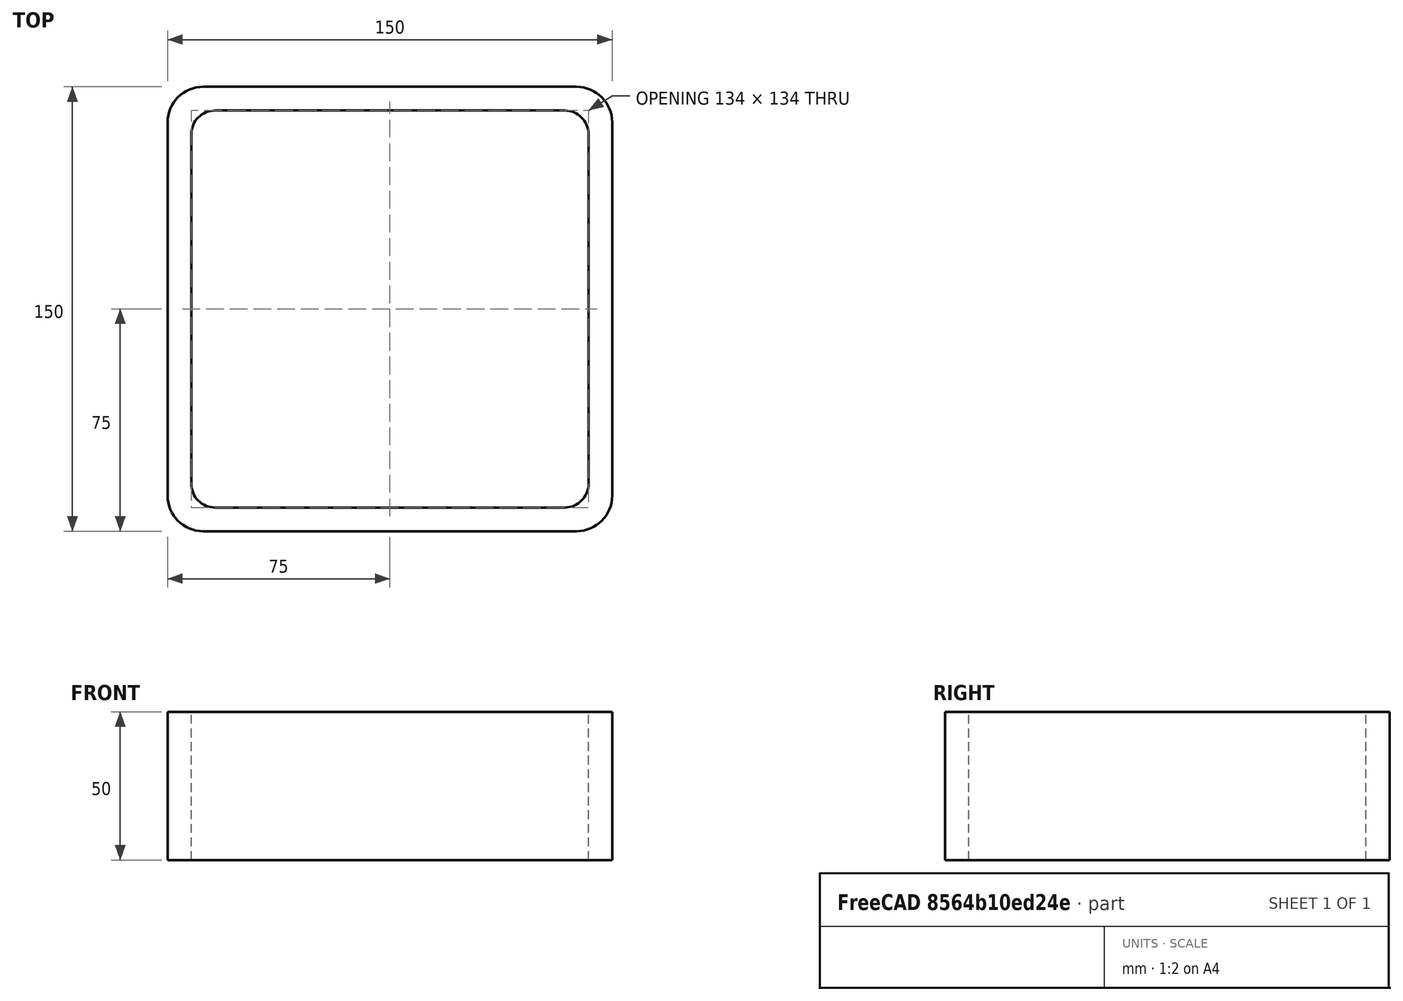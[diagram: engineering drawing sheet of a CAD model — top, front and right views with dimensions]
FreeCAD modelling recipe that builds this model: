
FCSTD DOCUMENT  (FreeCAD 0.15R4671 (Git))
Label: Square hollow section 150x150x8 EN10219 S235JRH
License: All rights reserved
LicenseURL: http://en.wikipedia.org/wiki/All_rights_reserved
objects: Sketcher::SketchObject×1, Part::Extrusion×1
note: 2 computed .brp shape members not serialized (recipe doc carries the construction recipe); baked Part::Feature solids carry a one-line shape summary decoded from their .brp

FEATURE [Sketcher::SketchObject] Sketch
  sketch-geometry (16):
    g0: LineSegment StartX=-59 StartY=67 StartZ=0 EndX=59 EndY=67 EndZ=0
    g1: LineSegment StartX=67 StartY=59 StartZ=0 EndX=67 EndY=-59 EndZ=0
    g2: LineSegment StartX=59 StartY=-67 StartZ=0 EndX=-59 EndY=-67 EndZ=0
    g3: LineSegment StartX=-67 StartY=-59 StartZ=0 EndX=-67 EndY=59 EndZ=0
    g4: LineSegment StartX=-63 StartY=75 StartZ=0 EndX=63 EndY=75 EndZ=0
    g5: LineSegment StartX=75 StartY=63 StartZ=0 EndX=75 EndY=-63 EndZ=0
    g6: LineSegment StartX=63 StartY=-75 StartZ=0 EndX=-63 EndY=-75 EndZ=0
    g7: LineSegment StartX=-75 StartY=-63 StartZ=0 EndX=-75 EndY=63 EndZ=0
    g8: ArcOfCircle CenterX=-59 CenterY=59 CenterZ=0 NormalX=0 NormalY=0 NormalZ=1 Radius=8 StartAngle=1.5708 EndAngle=3.14159
    g9: ArcOfCircle CenterX=59 CenterY=59 CenterZ=0 NormalX=0 NormalY=0 NormalZ=1 Radius=8 StartAngle=0 EndAngle=1.5708
    g10: ArcOfCircle CenterX=59 CenterY=-59 CenterZ=0 NormalX=0 NormalY=0 NormalZ=1 Radius=8 StartAngle=4.71239 EndAngle=6.28319
    g11: ArcOfCircle CenterX=-59 CenterY=-59 CenterZ=0 NormalX=0 NormalY=0 NormalZ=1 Radius=8 StartAngle=3.14159 EndAngle=4.71239
    g12: ArcOfCircle CenterX=63 CenterY=63 CenterZ=0 NormalX=0 NormalY=0 NormalZ=1 Radius=12 StartAngle=0 EndAngle=1.5708
    g13: ArcOfCircle CenterX=63 CenterY=-63 CenterZ=0 NormalX=0 NormalY=0 NormalZ=1 Radius=12 StartAngle=4.71239 EndAngle=6.28319
    g14: ArcOfCircle CenterX=-63 CenterY=-63 CenterZ=0 NormalX=0 NormalY=0 NormalZ=1 Radius=12 StartAngle=3.14159 EndAngle=4.71239
    g15: ArcOfCircle CenterX=-63 CenterY=63 CenterZ=0 NormalX=0 NormalY=0 NormalZ=1 Radius=12 StartAngle=1.5708 EndAngle=3.14159
  constraints (36):
    c: Horizontal(g2)
    c: Vertical(g3)
    c: Horizontal(g6)
    c: Vertical(g7)
    c: Tangent(g3,g8) = 1.5708
    c: Tangent(g0,g8) = 1.5708
    c: Tangent(g0,g9) = 1.5708
    c: Tangent(g1,g9) = 1.5708
    c: Tangent(g1,g10) = 1.5708
    c: Tangent(g2,g10) = 1.5708
    c: Tangent(g2,g11) = 1.5708
    c: Tangent(g3,g11) = 1.5708
    c: Tangent(g4,g12) = 1.5708
    c: Tangent(g5,g12) = 1.5708
    c: Tangent(g5,g13) = 1.5708
    c: Tangent(g6,g13) = 1.5708
    c: Tangent(g6,g14) = 1.5708
    c: Tangent(g7,g14) = 1.5708
    c: Tangent(g7,g15) = 1.5708
    c: Tangent(g4,g15) = 1.5708
    c: Equal(g9,g8)
    c: Equal(g9,g11)
    c: Equal(g9,g10)
    c: Equal(g12,g15)
    c: Equal(g12,g14)
    c: Equal(g12,g13)
    c: Symmetric(g4,g6,g-1)
    c: Symmetric(g7,g5,g-2)
    c: DistanceY(g4,g6) = -150
    c: DistanceX(g7,g5) = 150
    c: Symmetric(g3,g1,g-2)
    c: Symmetric(g0,g2,g-1)
    c: DistanceY(g0,g4) = 8
    c: DistanceX(g5,g1) = -8
    c: Radius(g9) = 8
    c: Radius(g12) = 12
FEATURE [Part::Extrusion] Extrude  label="Square hollow section 150x150x8 EN10219 S235JRH"
  Base = -> Sketch
  Dir = (0,0,50)
  Solid = true
